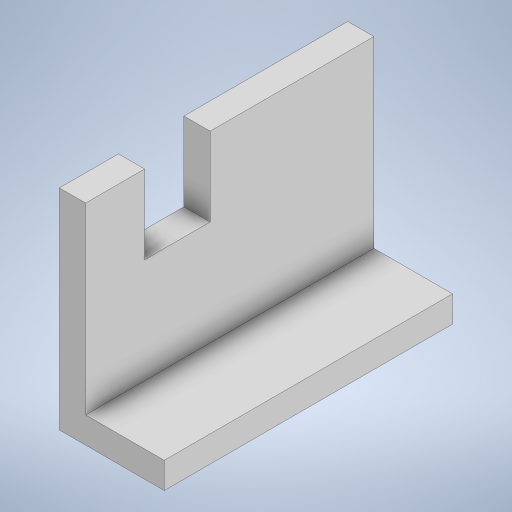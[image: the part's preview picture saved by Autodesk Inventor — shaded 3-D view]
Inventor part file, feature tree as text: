
AUTODESK INVENTOR PART (.ipt)
format: ipt  version: 2023 (Build 270158000, 158)  size: 212,480 bytes
history: native  units: in
note: dims shown in document units (in); Inventor stores cm internally (conversion verified against a paired STEP export)
features: extrude x2, sketch x2
ambient origin geometry x8: Origin, YZ Plane, XZ Plane, XY Plane, X Axis, Y Axis, Z Axis, Center Point
bodies: Solid1 (feature_tree)
feature tree (4):
  extrude  "Extrusion1"  Depth=0.6299in
  extrude  "Extrusion3"  Depth=0.8661in TaperAngle=0.0deg
  sketch  "Sketch1"  dims[d0=0.0787in d1=0.6299in]
  sketch  "Sketch3"  dims[d2=0.2362in d3=0.8661in d4=0.0in d9=0.1969in d10=0.2362in d11=0.3937in d12=0.0in]
